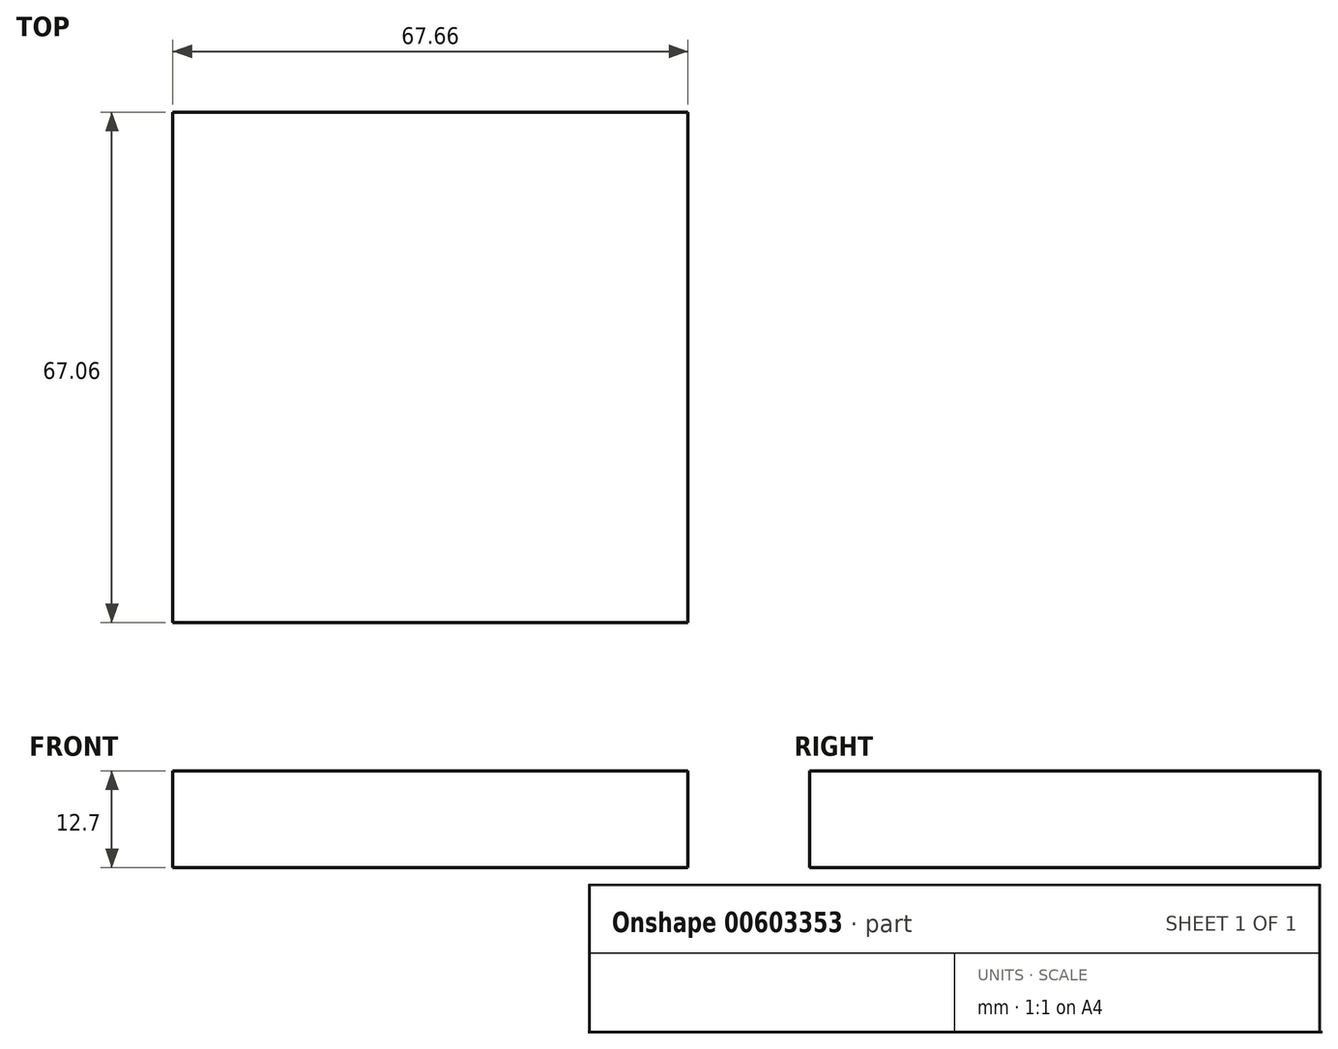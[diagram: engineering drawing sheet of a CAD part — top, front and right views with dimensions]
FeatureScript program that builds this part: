
annotation { "Feature Type Name" : "Feature", "Feature Type Description" : "" }
export const myFeature = defineFeature(function(context is Context, id is Id, definition is map)
    precondition{}
    {
        {
            var Q0;
            Q0=qCreatedBy(makeId("Top.planeOp"),FACE);
            var sketch = newSketch(context, id + "F0", { "sketchPlane" : qUnion([Q0])});
            skLineSegment(sketch, "E0.bottom", {"start": v(-75.74, 75.29) * mm, "end": v(-8.08, 75.29) * mm});
            skLineSegment(sketch, "E0.top", {"start": v(-75.74, 8.23) * mm, "end": v(-8.08, 8.23) * mm});
            skLineSegment(sketch, "E0.left", {"start": v(-75.74, 75.29) * mm, "end": v(-75.74, 8.23) * mm});
            skLineSegment(sketch, "E0.right", {"start": v(-8.08, 75.29) * mm, "end": v(-8.08, 8.23) * mm});
            skSolve(sketch);
        }
        {
            var Q0;
            Q0=makeQuery(id+"F0.imprint","IMPRINT",FACE,{"disambiguationData":[TD([[makeQuery(id+"F0.imprint","IMPRINT",EDGE,{"derivedFrom":sQuery(id+"F0.wireOp",EDGE,"E0.bottom")}),-1.0]])]});
            extrude(context, id + "F1", {"entities" : qUnion([Q0]), "depth" : 12.7 * mm, "offsetDistance" : 25.4 * mm});
        }
    });
